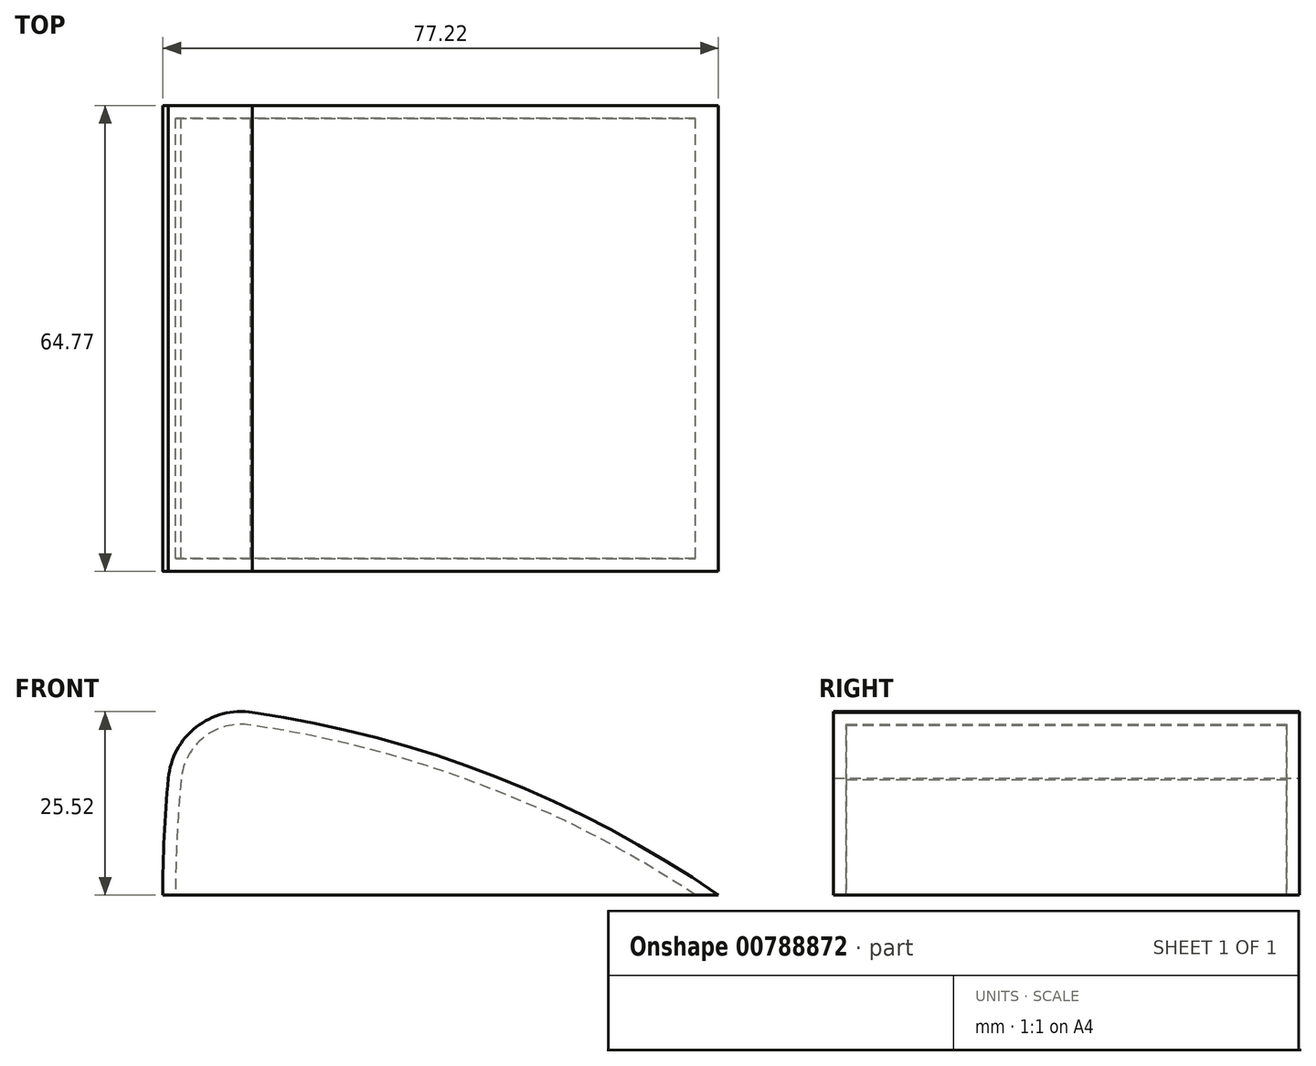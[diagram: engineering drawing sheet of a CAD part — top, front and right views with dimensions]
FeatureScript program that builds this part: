
annotation { "Feature Type Name" : "Feature", "Feature Type Description" : "" }
export const myFeature = defineFeature(function(context is Context, id is Id, definition is map)
    precondition{}
    {
        {
            var Q0;
            Q0=qCreatedBy(makeId("Front.planeOp"),FACE);
            var sketch = newSketch(context, id + "F0", { "sketchPlane" : qUnion([Q0])});
            skLineSegment(sketch, "E0", {"start": v(-29.8, 0) * mm, "end": v(47.42, 0) * mm});
            skArc(sketch, "E1", {"start": v(-29.03, 16.26) * mm, "mid": v(-29.63, 8.14) * mm, "end": v(-29.8, 0) * mm});
            skArc(sketch, "E2", {"start": v(47.42, 0) * mm, "mid": v(16.5, 16.45) * mm, "end": v(-17.35, 25.4) * mm});
            skArc(sketch, "E3", {"start": v(-17.35, 25.4) * mm, "mid": v(-25.17, 23.36) * mm, "end": v(-29.03, 16.26) * mm});
            skSolve(sketch);
        }
        {
            var Q0;
            Q0=makeQuery(id+"F0.imprint","IMPRINT",FACE,{"disambiguationData":[TD([[makeQuery(id+"F0.imprint","IMPRINT",EDGE,{"derivedFrom":sQuery(id+"F0.wireOp",EDGE,"E0")}),1.0]])]});
            extrude(context, id + "F1", {"entities" : qUnion([Q0]), "depth" : 64.77 * mm, "offsetDistance" : 25.4 * mm});
        }
        {
            var Q0;
            Q0=makeQuery(id+"F1.opExtrude","SWEPT_FACE",FACE,{"disambiguationData":[OSD([sQuery(id+"F0.wireOp",EDGE,"E0")])]});
            shell(context, id + "F2", {"entities" : qUnion([Q0]), "thickness" : 1.78 * mm});
        }
        {
            var Q0;
            Q0=makeQuery(id+"F1.opExtrude","SWEPT_FACE",FACE,{"disambiguationData":[OSD([sQuery(id+"F0.wireOp",EDGE,"E0")])]});
            cPlane(context, id + "F3", {"entities" : qUnion([Q0]), "cplaneType" : CPlaneType.OFFSET, "offset" : 0 * mm, "width" : 152.4 * mm, "height" : 152.4 * mm});
        }
    });
